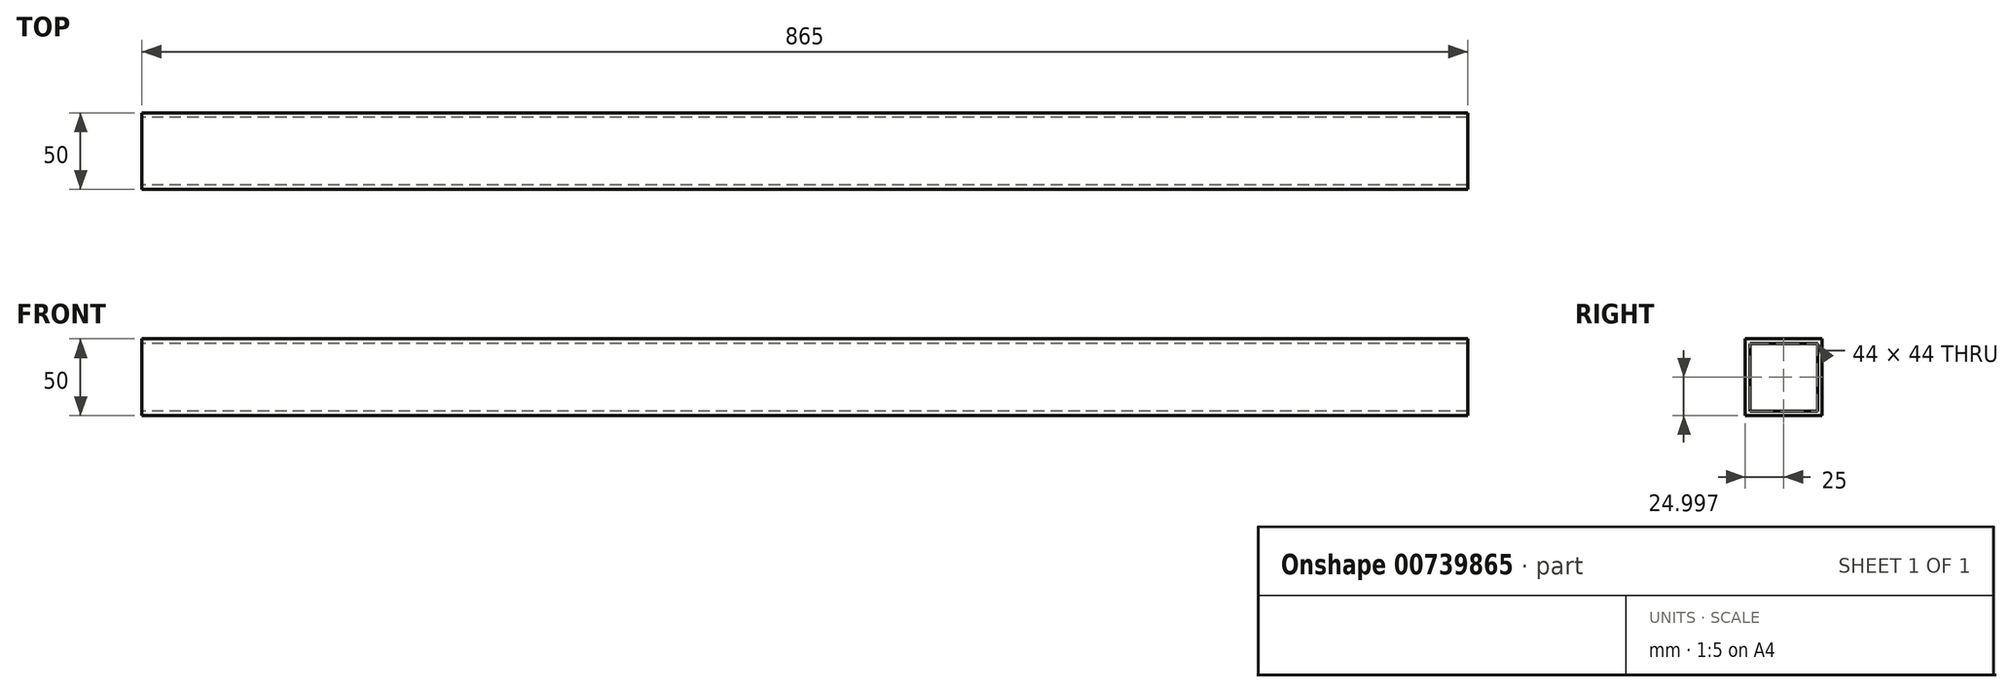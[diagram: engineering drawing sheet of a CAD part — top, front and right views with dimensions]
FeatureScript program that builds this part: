
annotation { "Feature Type Name" : "Feature", "Feature Type Description" : "" }
export const myFeature = defineFeature(function(context is Context, id is Id, definition is map)
    precondition{}
    {
        {
            var Q0;
            Q0=qCreatedBy(makeId("Right.planeOp"),FACE);
            var sketch = newSketch(context, id + "F0", { "sketchPlane" : qUnion([Q0])});
            skLineSegment(sketch, "E0.bottom", {"start": v(-45.22, -30.72) * mm, "end": v(-95.22, -30.72) * mm});
            skLineSegment(sketch, "E0.top", {"start": v(-45.22, 19.28) * mm, "end": v(-95.22, 19.28) * mm});
            skLineSegment(sketch, "E0.left", {"start": v(-45.22, -30.72) * mm, "end": v(-45.22, 19.28) * mm});
            skLineSegment(sketch, "E0.right", {"start": v(-95.22, -30.72) * mm, "end": v(-95.22, 19.28) * mm});
            skPoint(sketch, "E0.middle", {"position": v(-70.22, -5.72) * mm});
            skLineSegment(sketch, "E1.0", {"start": v(-92.22, -27.72) * mm, "end": v(-92.22, 16.28) * mm});
            skLineSegment(sketch, "E1.1", {"start": v(-48.22, -27.72) * mm, "end": v(-92.22, -27.72) * mm});
            skLineSegment(sketch, "E1.2", {"start": v(-48.22, -27.72) * mm, "end": v(-48.22, 16.28) * mm});
            skLineSegment(sketch, "E1.3", {"start": v(-48.22, 16.28) * mm, "end": v(-92.22, 16.28) * mm});
            skSolve(sketch);
        }
        {
            var Q0;
            Q0 = qSketchRegion(id + "F0", true);
            extrude(context, id + "F1", {"entities" : qUnion([Q0]), "depth" : 865 * mm, "offsetDistance" : 25 * mm});
        }
    });
